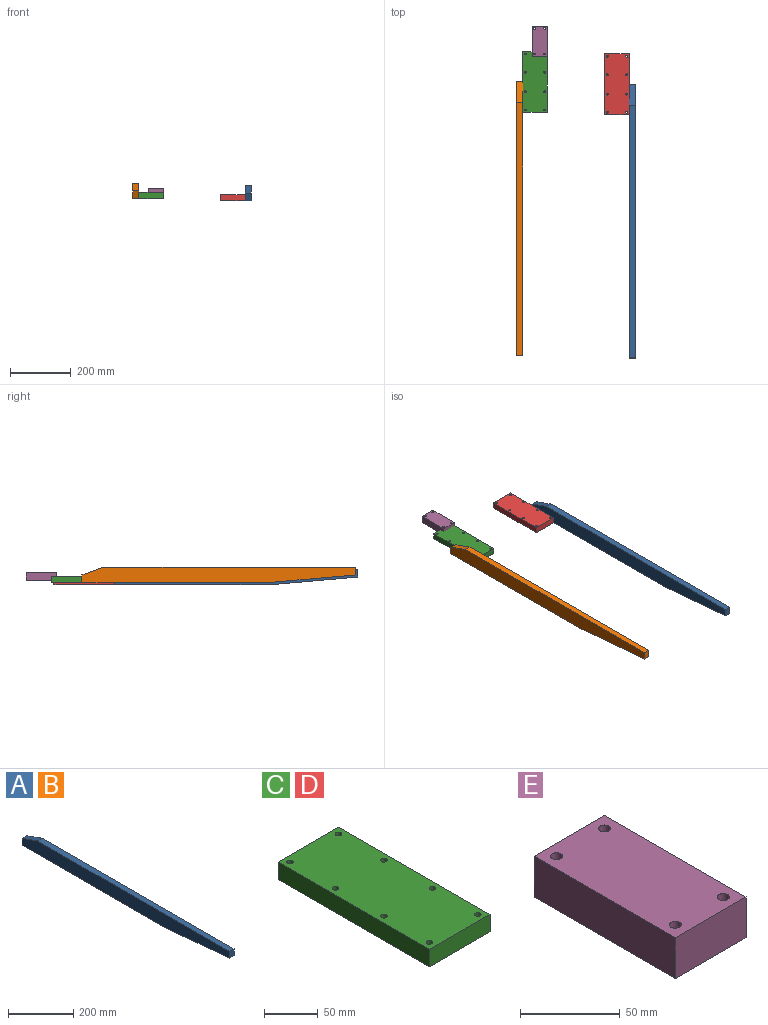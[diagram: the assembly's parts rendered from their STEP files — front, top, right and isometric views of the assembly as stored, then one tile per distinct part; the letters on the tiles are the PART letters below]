
ASSEMBLY  parts=5 mates=4
PART A: 8 faces, bbox 20x900x50 mm
  f0: plane 831.31x20mm, normal (0,0,1), area 16626.3mm2, adj f1,f5,f6,f7
  f1: plane 25x20mm, normal (0,-1,0), area 500mm2, adj f0,f2,f6,f7
  f2: plane 285.75x25mm, normal (0,-0.09,-1), area 5736.9mm2, adj f1,f3,f6,f7
  f3: plane 614.25x20mm, normal (0,0,-1), area 12285mm2, adj f2,f4,f6,f7
  f4: plane 25x20mm, normal (0,1,0), area 500mm2, adj f3,f5,f6,f7
  f5: plane 68.69x25mm, normal (0,0.34,0.94), area 1461.9mm2, adj f0,f4,f6,f7
  f6: plane 900x50mm, normal (1,0,0), area 40569.5mm2, adj f0,f1,f2,f3,f4,f5
  f7: plane 900x50mm, normal (-1,0,0), area 40569.5mm2, adj f0,f1,f2,f3,f4,f5
PART B: same geometry as A
PART C: 14 faces, bbox 80x200x20 mm
  f0: plane 200x20mm, normal (-1,0,0), area 4000mm2, adj f1,f10,f12,f13
  f1: plane 80x20mm, normal (0,-1,0), area 1600mm2, adj f0,f2,f12,f13
  f2: plane 200x20mm, normal (1,0,0), area 4000mm2, adj f1,f10,f12,f13
  f3: cylinder r=3mm len=20mm, axis (0,0,1), area 377mm2, adj f12,f13
  f4: cylinder r=3mm len=20mm, axis (0,0,1), area 377mm2, adj f12,f13
  f5: cylinder r=3mm len=20mm, axis (0,0,1), area 377mm2, adj f12,f13
  f6: cylinder r=3mm len=20mm, axis (0,0,1), area 377mm2, adj f12,f13
  f7: cylinder r=3mm len=20mm, axis (0,0,1), area 377mm2, adj f12,f13
  f8: cylinder r=3mm len=20mm, axis (0,0,1), area 377mm2, adj f12,f13
  f9: cylinder r=3mm len=20mm, axis (0,0,1), area 377mm2, adj f12,f13
  f10: plane 80x20mm, normal (0,1,0), area 1600mm2, adj f0,f2,f12,f13
  f11: cylinder r=3mm len=20mm, axis (0,0,1), area 377mm2, adj f12,f13
  f12: plane 200x80mm, normal (0,0,-1), area 15773.8mm2, adj f0,f1,f2,f3,f4,f5,f6,f7
  f13: plane 200x80mm, normal (0,0,1), area 15773.8mm2, adj f0,f1,f2,f3,f4,f5,f6,f7
PART D: same geometry as C
PART E: 10 faces, bbox 50x100x25 mm
  f0: plane 50x25mm, normal (0,1,0), area 1250mm2, adj f1,f6,f8,f9
  f1: plane 100x25mm, normal (-1,0,0), area 2500mm2, adj f0,f2,f8,f9
  f2: plane 50x25mm, normal (0,-1,0), area 1250mm2, adj f1,f6,f8,f9
  f3: cylinder r=3mm len=25mm, axis (0,0,-1), area 471.2mm2, adj f8,f9
  f4: cylinder r=3mm len=25mm, axis (0,0,-1), area 471.2mm2, adj f8,f9
  f5: cylinder r=3mm len=25mm, axis (0,0,-1), area 471.2mm2, adj f8,f9
  f6: plane 100x25mm, normal (1,0,0), area 2500mm2, adj f0,f2,f8,f9
  f7: cylinder r=3mm len=25mm, axis (0,0,-1), area 471.2mm2, adj f8,f9
  f8: plane 100x50mm, normal (0,0,1), area 4886.9mm2, adj f0,f1,f2,f3,f4,f5,f6,f7
  f9: plane 100x50mm, normal (0,0,-1), area 4886.9mm2, adj f0,f1,f2,f3,f4,f5,f6,f7
PLACE A t=(292.3,-460.4,47.95)mm
PLACE B t=(-77.12,-452.4,54.92)mm
PLACE C rot(axis=(1,0,0),180deg) t=(22.88,381.9,-14.61)mm
PLACE D t=(292.3,-307.84,-1.59)mm
PLACE E t=(88.56,145.58,-7.11)mm
MATE fastened A.f7 <-> D.f2  axis (-1,0,0) through (292.3,33.03,-21.59)mm
MATE parallel C.f3 <-> E.f7  axis (0,0,1) through (14.88,133.03,5.39)mm
MATE parallel C.f2 <-> D.f0  axis (1,0,0) through (22.88,41.03,-4.61)mm
MATE fastened B.f6 <-> C.f0  axis (1,0,0) through (-57.12,41.03,-14.61)mm
